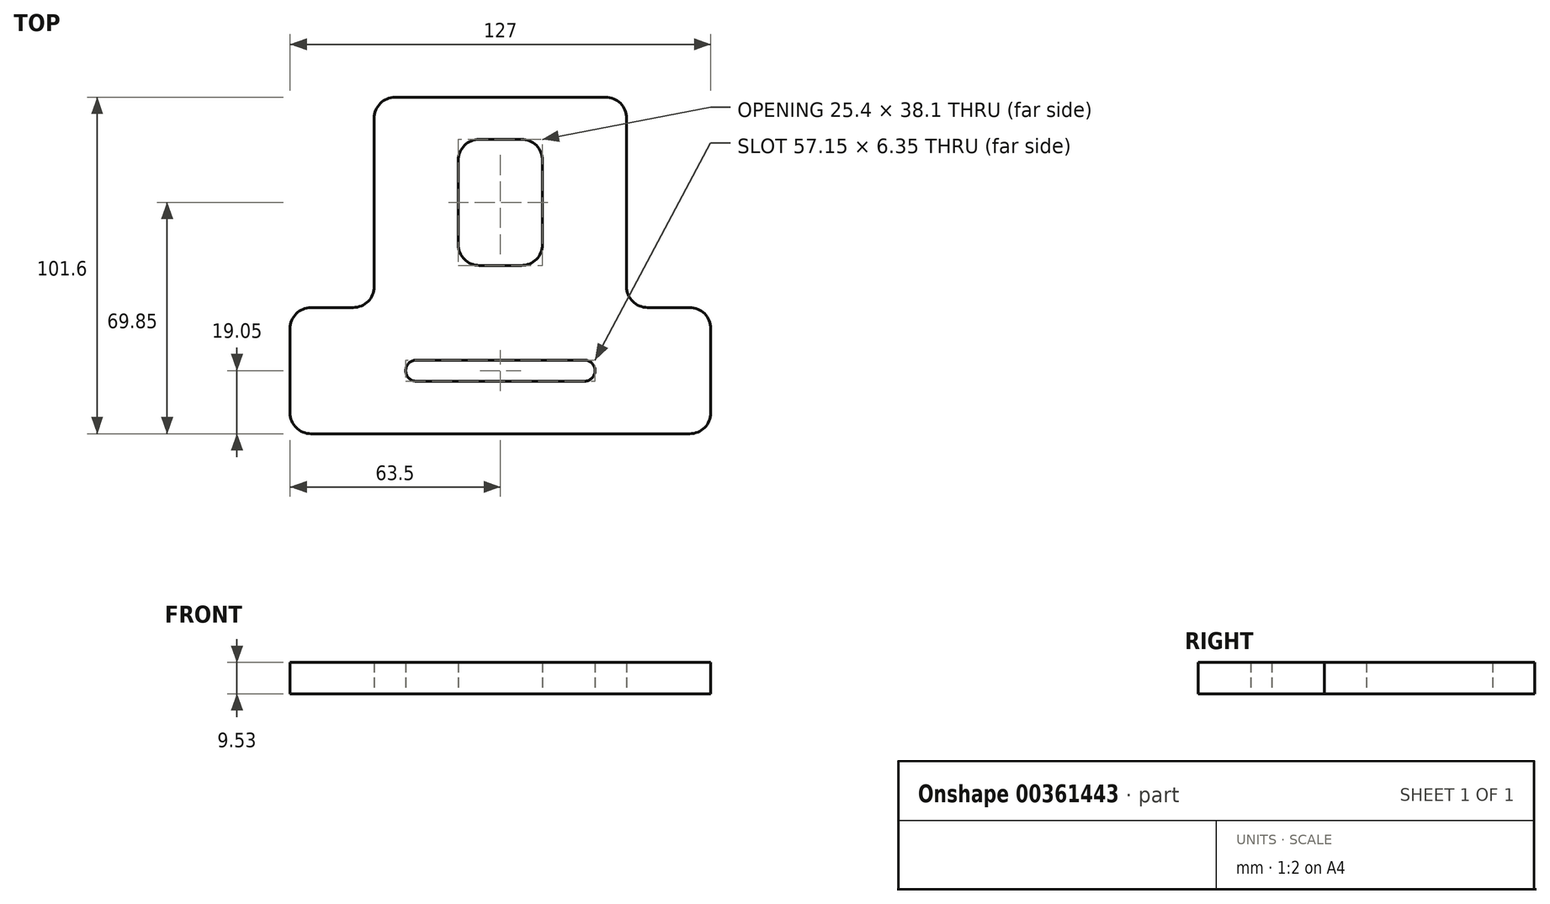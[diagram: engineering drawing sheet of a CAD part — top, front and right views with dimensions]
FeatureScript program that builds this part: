
annotation { "Feature Type Name" : "Feature", "Feature Type Description" : "" }
export const myFeature = defineFeature(function(context is Context, id is Id, definition is map)
    precondition{}
    {
        {
            var Q0;
            Q0=qCreatedBy(makeId("Top.planeOp"),FACE);
            var sketch = newSketch(context, id + "F0", { "sketchPlane" : qUnion([Q0])});
            skLineSegment(sketch, "E0.bottom", {"start": v(57.15, -50.8) * mm, "end": v(-57.15, -50.8) * mm});
            skLineSegment(sketch, "E0.top", {"start": v(31.75, 50.8) * mm, "end": v(-31.75, 50.8) * mm});
            skLineSegment(sketch, "E0.left", {"start": v(63.5, -44.45) * mm, "end": v(63.5, -19.05) * mm});
            skLineSegment(sketch, "E0.right", {"start": v(-63.5, -44.45) * mm, "end": v(-63.5, -19.05) * mm});
            skPoint(sketch, "E0.middle", {"position": v(0, 0) * mm});
            skLineSegment(sketch, "E1", {"start": v(-57.15, -12.7) * mm, "end": v(-44.45, -12.7) * mm});
            skLineSegment(sketch, "E2", {"start": v(-38.1, -6.35) * mm, "end": v(-38.1, 44.45) * mm});
            skPoint(sketch, "E3.orphan", {"position": v(-63.5, 50.8) * mm});
            skLineSegment(sketch, "E4", {"start": v(57.15, -12.7) * mm, "end": v(44.45, -12.7) * mm});
            skLineSegment(sketch, "E5", {"start": v(38.1, -6.35) * mm, "end": v(38.1, 44.45) * mm});
            skPoint(sketch, "E6.orphan", {"position": v(63.5, 50.8) * mm});
            skLineSegment(sketch, "E7.bottom", {"start": v(6.35, 0) * mm, "end": v(-6.35, 0) * mm});
            skLineSegment(sketch, "E7.top", {"start": v(6.35, 38.1) * mm, "end": v(-6.35, 38.1) * mm});
            skLineSegment(sketch, "E7.left", {"start": v(12.7, 6.35) * mm, "end": v(12.7, 31.75) * mm});
            skLineSegment(sketch, "E7.right", {"start": v(-12.7, 6.35) * mm, "end": v(-12.7, 31.75) * mm});
            skPoint(sketch, "E7.middle", {"position": v(0, 19.05) * mm});
            skArc(sketch, "E8", {"start": v(25.4, -34.92) * mm, "mid": v(28.58, -31.75) * mm, "end": v(25.4, -28.57) * mm});
            skArc(sketch, "E9", {"start": v(-25.4, -28.57) * mm, "mid": v(-28.57, -31.75) * mm, "end": v(-25.4, -34.92) * mm});
            skLineSegment(sketch, "E10", {"start": v(-25.4, -28.57) * mm, "end": v(25.4, -28.57) * mm});
            skLineSegment(sketch, "E11", {"start": v(-25.4, -34.92) * mm, "end": v(25.4, -34.92) * mm});
            skPoint(sketch, "E12.visualSharp", {"position": v(-38.1, 50.8) * mm});
            skArc(sketch, "E12.filletArc", {"start": v(-31.75, 50.8) * mm, "mid": v(-36.24, 48.94) * mm, "end": v(-38.1, 44.45) * mm});
            skPoint(sketch, "E13.visualSharp", {"position": v(38.1, 50.8) * mm});
            skArc(sketch, "E13.filletArc", {"start": v(38.1, 44.45) * mm, "mid": v(36.24, 48.94) * mm, "end": v(31.75, 50.8) * mm});
            skPoint(sketch, "E14.visualSharp", {"position": v(38.1, -12.7) * mm});
            skArc(sketch, "E14.filletArc", {"start": v(38.1, -6.35) * mm, "mid": v(39.96, -10.84) * mm, "end": v(44.45, -12.7) * mm});
            skPoint(sketch, "E15.visualSharp", {"position": v(63.5, -12.7) * mm});
            skArc(sketch, "E15.filletArc", {"start": v(63.5, -19.05) * mm, "mid": v(61.64, -14.56) * mm, "end": v(57.15, -12.7) * mm});
            skPoint(sketch, "E16.visualSharp", {"position": v(63.5, -50.8) * mm});
            skArc(sketch, "E16.filletArc", {"start": v(57.15, -50.8) * mm, "mid": v(61.64, -48.94) * mm, "end": v(63.5, -44.45) * mm});
            skPoint(sketch, "E17.visualSharp", {"position": v(-63.5, -50.8) * mm});
            skArc(sketch, "E17.filletArc", {"start": v(-63.5, -44.45) * mm, "mid": v(-61.64, -48.94) * mm, "end": v(-57.15, -50.8) * mm});
            skPoint(sketch, "E18.visualSharp", {"position": v(-63.5, -12.7) * mm});
            skArc(sketch, "E18.filletArc", {"start": v(-57.15, -12.7) * mm, "mid": v(-61.64, -14.56) * mm, "end": v(-63.5, -19.05) * mm});
            skPoint(sketch, "E19.visualSharp", {"position": v(-38.1, -12.7) * mm});
            skArc(sketch, "E19.filletArc", {"start": v(-44.45, -12.7) * mm, "mid": v(-39.96, -10.84) * mm, "end": v(-38.1, -6.35) * mm});
            skPoint(sketch, "E20.visualSharp", {"position": v(-12.7, 0) * mm});
            skArc(sketch, "E20.filletArc", {"start": v(-12.7, 6.35) * mm, "mid": v(-10.84, 1.86) * mm, "end": v(-6.35, 0) * mm});
            skPoint(sketch, "E21.visualSharp", {"position": v(12.7, 0) * mm});
            skArc(sketch, "E21.filletArc", {"start": v(6.35, 0) * mm, "mid": v(10.84, 1.86) * mm, "end": v(12.7, 6.35) * mm});
            skPoint(sketch, "E22.visualSharp", {"position": v(12.7, 38.1) * mm});
            skArc(sketch, "E22.filletArc", {"start": v(12.7, 31.75) * mm, "mid": v(10.84, 36.24) * mm, "end": v(6.35, 38.1) * mm});
            skPoint(sketch, "E23.visualSharp", {"position": v(-12.7, 38.1) * mm});
            skArc(sketch, "E23.filletArc", {"start": v(-6.35, 38.1) * mm, "mid": v(-10.84, 36.24) * mm, "end": v(-12.7, 31.75) * mm});
            skSolve(sketch);
        }
        {
            var Q0;
            Q0=makeQuery(id+"F0.imprint","IMPRINT",FACE,{"disambiguationData":[TD([[makeQuery(id+"F0.imprint","IMPRINT",EDGE,{"derivedFrom":sQuery(id+"F0.wireOp",EDGE,"E0.bottom")}),-1.0]])]});
            extrude(context, id + "F1", {"entities" : qUnion([Q0]), "depth" : 9.52 * mm});
        }
    });
